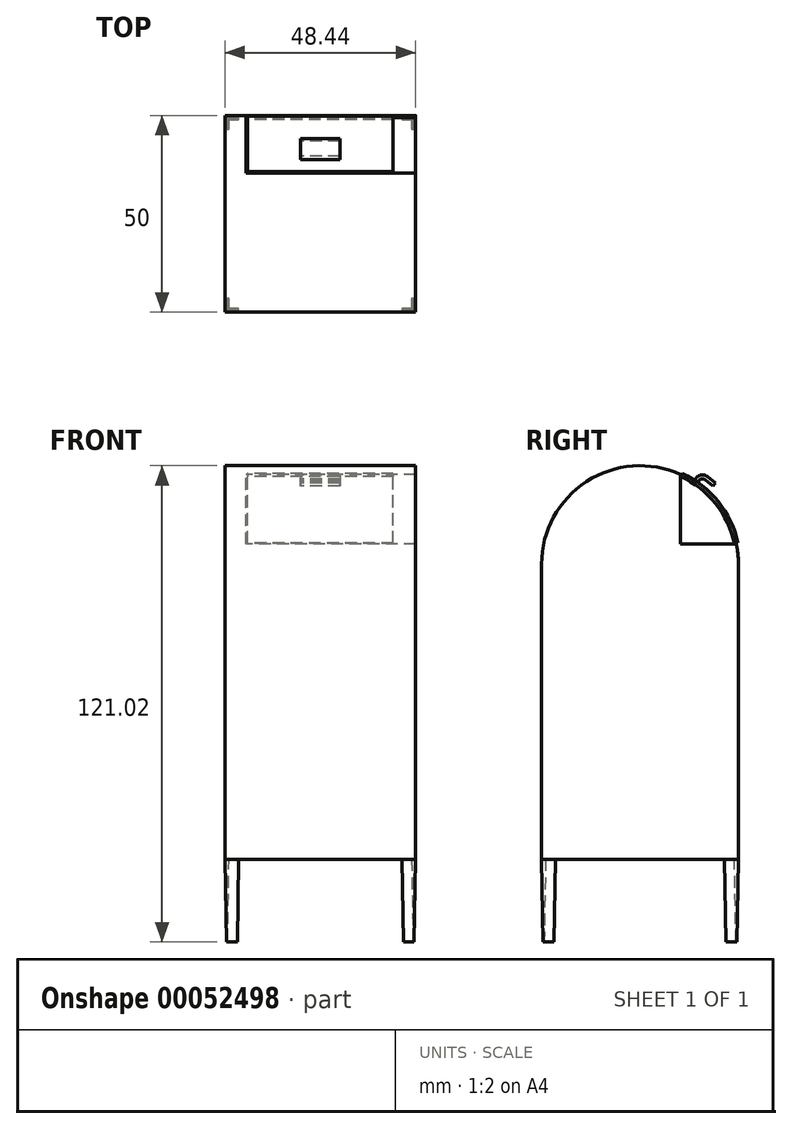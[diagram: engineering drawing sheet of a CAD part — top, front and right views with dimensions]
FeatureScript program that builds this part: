
annotation { "Feature Type Name" : "Feature", "Feature Type Description" : "" }
export const myFeature = defineFeature(function(context is Context, id is Id, definition is map)
    precondition{}
    {
        {
            var Q0;
            Q0=qCreatedBy(makeId("Right.planeOp"),FACE);
            var sketch = newSketch(context, id + "F0", { "sketchPlane" : qUnion([Q0])});
            skLineSegment(sketch, "E0.bottom", {"start": v(-25, 0) * mm, "end": v(25, 0) * mm});
            skLineSegment(sketch, "E0.top", {"start": v(0, 100) * mm, "end": v(0, 100) * mm});
            skLineSegment(sketch, "E0.left", {"start": v(-25, 0) * mm, "end": v(-25, 75) * mm});
            skLineSegment(sketch, "E0.right", {"start": v(25, 0) * mm, "end": v(25, 75) * mm});
            skPoint(sketch, "E1.visualSharp", {"position": v(-25, 100) * mm});
            skArc(sketch, "E1.filletArc", {"start": v(0, 100) * mm, "mid": v(-17.68, 92.68) * mm, "end": v(-25, 75) * mm});
            skPoint(sketch, "E2.visualSharp", {"position": v(25, 100) * mm});
            skArc(sketch, "E2.filletArc", {"start": v(25, 75) * mm, "mid": v(17.68, 92.68) * mm, "end": v(0, 100) * mm});
            skSolve(sketch);
        }
        {
            var Q0;
            Q0 = qSketchRegion(id + "F0", true);
            extrude(context, id + "F1", {"entities" : qUnion([Q0]), "endBound" : BoundingType.SYMMETRIC, "depth" : 48.44 * mm});
        }
        {
            var Q0;
            Q0=makeQuery(id+"F1.opExtrude","SWEPT_FACE",FACE,{"disambiguationData":[OSD([sQuery(id+"F0.wireOp",EDGE,"E0.bottom")])]});
            var sketch = newSketch(context, id + "F2", { "sketchPlane" : qUnion([Q0])});
            skLineSegment(sketch, "E3.0", {"start": v(24.22, 25) * mm, "end": v(20.72, 25) * mm});
            skLineSegment(sketch, "E3.1", {"start": v(24.22, 25) * mm, "end": v(24.22, 21.5) * mm});
            skLineSegment(sketch, "E3.2", {"start": v(24.22, -25) * mm, "end": v(20.72, -25) * mm});
            skLineSegment(sketch, "E3.3", {"start": v(-24.22, 25) * mm, "end": v(-24.22, 21.5) * mm});
            skLineSegment(sketch, "E4.0", {"start": v(23.22, 24) * mm, "end": v(23.22, 21.5) * mm});
            skLineSegment(sketch, "E4.1", {"start": v(23.22, 24) * mm, "end": v(20.72, 24) * mm});
            skLineSegment(sketch, "E4.2", {"start": v(-23.22, 24) * mm, "end": v(-23.22, 21.5) * mm});
            skLineSegment(sketch, "E4.3", {"start": v(23.22, -24) * mm, "end": v(20.72, -24) * mm});
            skLineSegment(sketch, "E5", {"start": v(24.22, 21.5) * mm, "end": v(23.22, 21.5) * mm});
            skLineSegment(sketch, "E6", {"start": v(24.22, -21.5) * mm, "end": v(23.22, -21.5) * mm});
            skLineSegment(sketch, "E7", {"start": v(-20.72, -25) * mm, "end": v(-20.72, -24) * mm});
            skLineSegment(sketch, "E8", {"start": v(20.72, 25) * mm, "end": v(20.72, 24) * mm});
            skLineSegment(sketch, "E9", {"start": v(0, 0) * mm, "end": v(0, -9.6) * mm, "construction": true});
            skLineSegment(sketch, "E10", {"start": v(0, 0) * mm, "end": v(8.39, 0) * mm, "construction": true});
            skLineSegment(sketch, "E11.trimOffspring", {"start": v(-23.22, 21.5) * mm, "end": v(-24.22, 21.5) * mm});
            skLineSegment(sketch, "E12.trimOffspring", {"start": v(24.22, -21.5) * mm, "end": v(24.22, -25) * mm});
            skLineSegment(sketch, "E13.trimOffspring", {"start": v(23.22, -21.5) * mm, "end": v(23.22, -24) * mm});
            skLineSegment(sketch, "E14.trimOffspring", {"start": v(20.72, -24) * mm, "end": v(20.72, -25) * mm});
            skLineSegment(sketch, "E15.trimOffspring", {"start": v(-20.72, 24) * mm, "end": v(-23.22, 24) * mm});
            skLineSegment(sketch, "E16.trimOffspring", {"start": v(-20.72, 25) * mm, "end": v(-24.22, 25) * mm});
            skLineSegment(sketch, "E17.trimOffspring", {"start": v(-20.72, 24) * mm, "end": v(-20.72, 25) * mm});
            skLineSegment(sketch, "E18.trimOffspring", {"start": v(-23.22, -21.5) * mm, "end": v(-23.22, -24) * mm});
            skLineSegment(sketch, "E19.trimOffspring", {"start": v(-24.22, -21.5) * mm, "end": v(-24.22, -25) * mm});
            skLineSegment(sketch, "E20.trimOffspring", {"start": v(-23.22, -21.5) * mm, "end": v(-24.22, -21.5) * mm});
            skLineSegment(sketch, "E21.trimOffspring", {"start": v(-20.72, -24) * mm, "end": v(-23.22, -24) * mm});
            skLineSegment(sketch, "E22.trimOffspring", {"start": v(-20.72, -25) * mm, "end": v(-24.22, -25) * mm});
            skSolve(sketch);
        }
        {
            var Q0;
            Q0 = qSketchRegion(id + "F2", true);
            extrude(context, id + "F3", {"entities" : qUnion([Q0]), "operationType" : NewBodyOperationType.ADD, "depth" : 21.02 * mm, "hasDraft" : true, "draftAngle" : 1 * degree, "draftPullDirection" : true});
        }
        {
            var Q0;
            Q0=qCreatedBy(makeId("Right.planeOp"),FACE);
            var sketch = newSketch(context, id + "F4", { "sketchPlane" : qUnion([Q0])});
            skLineSegment(sketch, "E23.bottom", {"start": v(10.3, 80.06) * mm, "end": v(57.17, 80.06) * mm});
            skLineSegment(sketch, "E23.top", {"start": v(10.3, 106.21) * mm, "end": v(57.17, 106.21) * mm});
            skLineSegment(sketch, "E23.left", {"start": v(10.3, 80.06) * mm, "end": v(10.3, 106.21) * mm});
            skLineSegment(sketch, "E23.right", {"start": v(57.17, 80.06) * mm, "end": v(57.17, 106.21) * mm});
            skSolve(sketch);
        }
        {
            var Q0;
            Q0 = qSketchRegion(id + "F4", true);
            extrude(context, id + "F5", {"entities" : qUnion([Q0]), "operationType" : NewBodyOperationType.REMOVE, "depth" : 25 * mm});
        }
        {
            var Q0;
            Q0 = qSketchRegion(id + "F4", true);
            extrude(context, id + "F6", {"entities" : qUnion([Q0]), "operationType" : NewBodyOperationType.REMOVE, "endBound" : BoundingType.SYMMETRIC, "oppositeDirection" : true, "depth" : 37.84 * mm});
        }
        {
            var Q0;
            Q0=qCreatedBy(makeId("Right.planeOp"),FACE);
            var sketch = newSketch(context, id + "F7", { "sketchPlane" : qUnion([Q0])});
            skArc(sketch, "E24", {"start": v(24.43, 80.3) * mm, "mid": v(19.52, 90.62) * mm, "end": v(10.52, 97.68) * mm, "construction": true});
            skArc(sketch, "E25", {"start": v(24.48, 80.06) * mm, "mid": v(24.87, 77.54) * mm, "end": v(25, 75) * mm, "construction": true});
            skArc(sketch, "E26", {"start": v(-25, 75) * mm, "mid": v(-13.56, 96) * mm, "end": v(10.3, 97.78) * mm, "construction": true});
            skArc(sketch, "E27.0.startCap", {"start": v(24.87, 80.4) * mm, "mid": v(24.53, 79.87) * mm, "end": v(24, 80.21) * mm, "construction": true});
            skArc(sketch, "E27.0.endCap", {"start": v(10.33, 97.27) * mm, "mid": v(10.11, 97.87) * mm, "end": v(10.71, 98.09) * mm, "construction": true});
            skArc(sketch, "E27.0.left", {"start": v(24, 80.21) * mm, "mid": v(19.16, 90.34) * mm, "end": v(10.33, 97.27) * mm});
            skArc(sketch, "E27.0.right", {"start": v(24.87, 80.4) * mm, "mid": v(19.87, 90.9) * mm, "end": v(10.71, 98.09) * mm});
            skLineSegment(sketch, "E28", {"start": v(10.71, 98.09) * mm, "end": v(10.33, 97.27) * mm});
            skLineSegment(sketch, "E29", {"start": v(24, 80.21) * mm, "end": v(24.87, 80.4) * mm});
            skSolve(sketch);
        }
        {
            var Q0;
            Q0 = qSketchRegion(id + "F7", true);
            extrude(context, id + "F8", {"entities" : qUnion([Q0]), "operationType" : NewBodyOperationType.ADD, "endBound" : BoundingType.SYMMETRIC, "depth" : 36.97 * mm});
        }
        {
            var Q0;
            Q0=qCreatedBy(makeId("Right.planeOp"),FACE);
            var sketch = newSketch(context, id + "F9", { "sketchPlane" : qUnion([Q0])});
            skLineSegment(sketch, "E30", {"start": v(14.37, 95.45) * mm, "end": v(15.06, 96.31) * mm});
            skLineSegment(sketch, "E31", {"start": v(16.47, 96.47) * mm, "end": v(18.52, 94.83) * mm});
            skPoint(sketch, "E32.visualSharp", {"position": v(15.69, 97.1) * mm});
            skArc(sketch, "E32.filletArc", {"start": v(16.47, 96.47) * mm, "mid": v(15.73, 96.68) * mm, "end": v(15.06, 96.31) * mm});
            skLineSegment(sketch, "E33.0", {"start": v(17.1, 97.25) * mm, "end": v(19.14, 95.6) * mm});
            skArc(sketch, "E33.1", {"start": v(17.1, 97.25) * mm, "mid": v(15.62, 97.68) * mm, "end": v(14.28, 96.94) * mm});
            skLineSegment(sketch, "E33.2", {"start": v(13.6, 96.08) * mm, "end": v(14.28, 96.94) * mm});
            skLineSegment(sketch, "E34", {"start": v(13.6, 96.08) * mm, "end": v(14.37, 95.45) * mm});
            skLineSegment(sketch, "E35", {"start": v(18.52, 94.83) * mm, "end": v(19.14, 95.6) * mm});
            skSolve(sketch);
        }
        {
            var Q0;
            Q0 = qSketchRegion(id + "F9", true);
            extrude(context, id + "F10", {"entities" : qUnion([Q0]), "operationType" : NewBodyOperationType.ADD, "endBound" : BoundingType.SYMMETRIC, "depth" : 10.03 * mm});
        }
    });
